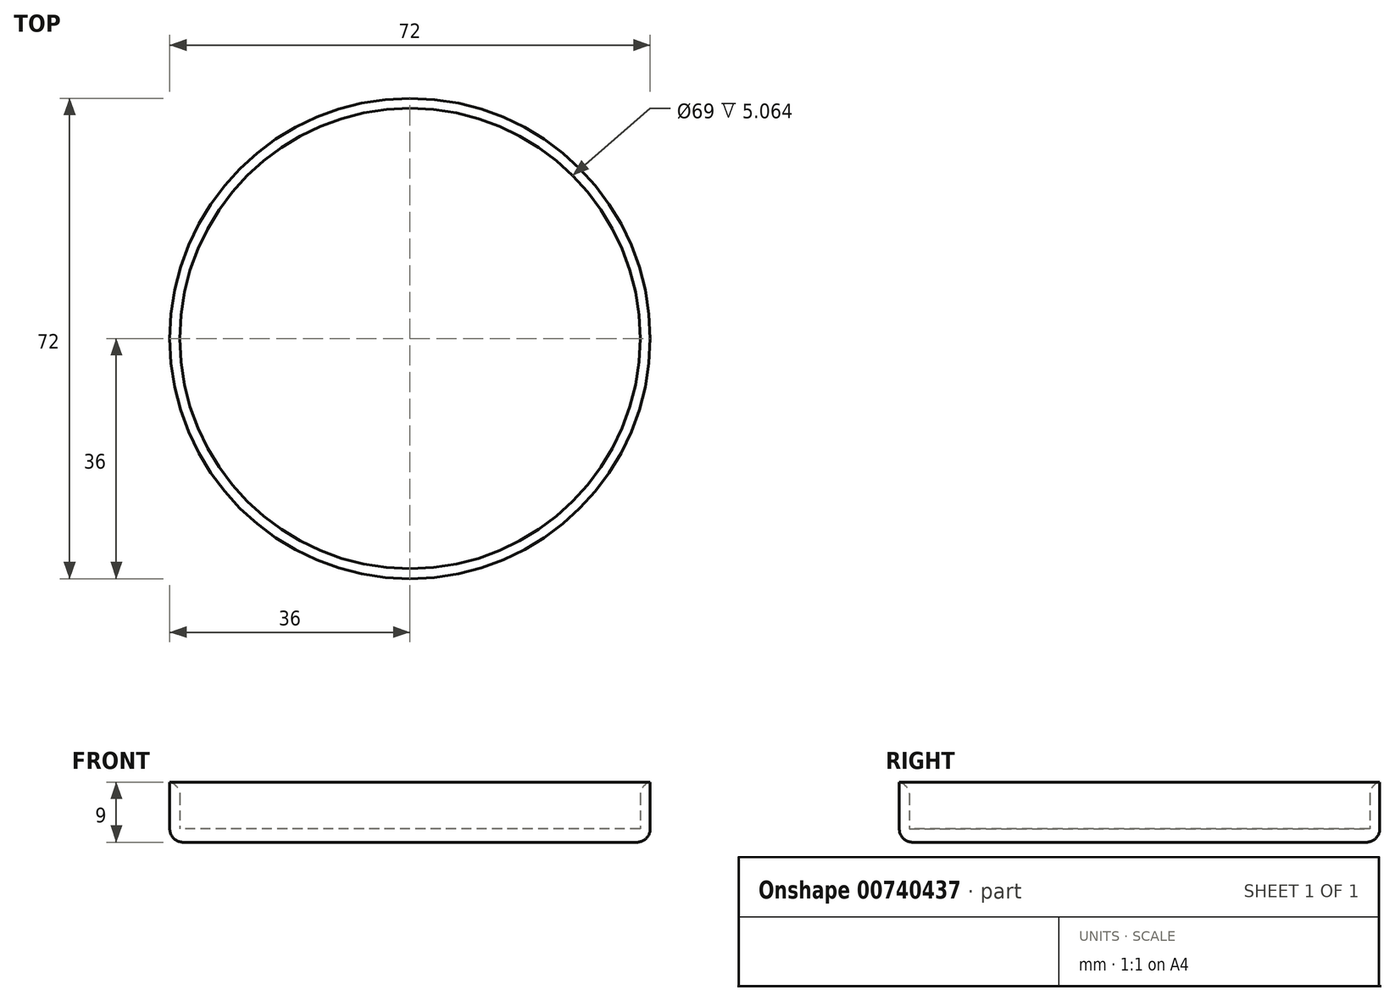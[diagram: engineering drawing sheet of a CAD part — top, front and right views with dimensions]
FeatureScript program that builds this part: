
annotation { "Feature Type Name" : "Feature", "Feature Type Description" : "" }
export const myFeature = defineFeature(function(context is Context, id is Id, definition is map)
    precondition{}
    {
        {
            var Q0;
            Q0=qCreatedBy(makeId("Top.planeOp"),FACE);
            var sketch = newSketch(context, id + "F0", { "sketchPlane" : qUnion([Q0])});
            skCircle(sketch, "E0", {"center": v(0, 0) * mm, "radius": 36 * mm});
            skCircle(sketch, "E1", {"center": v(0, 0) * mm, "radius": 34.5 * mm});
            skSolve(sketch);
        }
        {
            var Q0;
            Q0=makeQuery(id+"F0.imprint","IMPRINT",FACE,{"disambiguationData":[TD([[makeQuery(id+"F0.imprint","IMPRINT",EDGE,{"derivedFrom":sQuery(id+"F0.wireOp",EDGE,"E1")}),1.0]])]});
            extrude(context, id + "F1", {"entities" : qUnion([Q0]), "depth" : 2 * mm, "offsetDistance" : 25 * mm});
        }
        {
            var Q0;
            Q0=makeQuery(id+"F0.imprint","IMPRINT",FACE,{"disambiguationData":[TD([[makeQuery(id+"F0.imprint","IMPRINT",EDGE,{"derivedFrom":sQuery(id+"F0.wireOp",EDGE,"E0")}),1.0]])]});
            extrude(context, id + "F2", {"entities" : qUnion([Q0]), "operationType" : NewBodyOperationType.ADD, "depth" : 9 * mm, "offsetDistance" : 25 * mm});
        }
        {
            var Q0;
            Q0=makeQuery(id+"F2.opExtrude","CAP_EDGE",EDGE,{"disambiguationData":[OSD([sQuery(id+"F0.wireOp",EDGE,"E1")])],"isStart":false});
            var Q1;
            Q1=makeQuery(id+"F1.opExtrude","CAP_EDGE",EDGE,{"disambiguationData":[OSD([sQuery(id+"F0.wireOp",EDGE,"E1")])],"isStart":false});
            fillet(context, id + "F3", {"entities" : qUnion([Q0, Q1]), "radius" : 2 * mm, "tangentPropagation" : true, "allowEdgeOverflow" : false});
        }
        {
            var Q0;
            Q0=makeQuery(id+"F2.opExtrude","CAP_EDGE",EDGE,{"disambiguationData":[OSD([sQuery(id+"F0.wireOp",EDGE,"E0")])],"isStart":true});
            fillet(context, id + "F4", {"entities" : qUnion([Q0]), "radius" : 2 * mm, "tangentPropagation" : true, "allowEdgeOverflow" : false});
        }
    });
